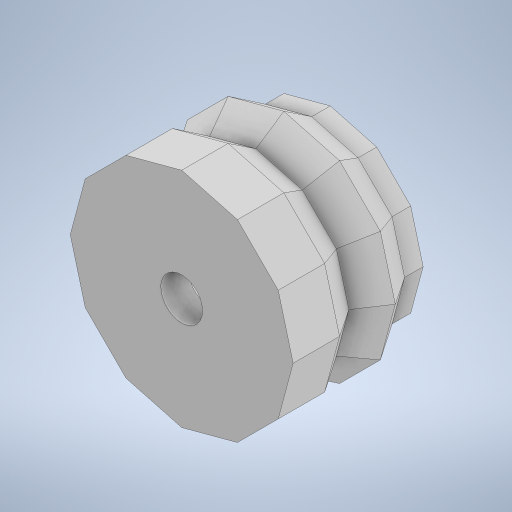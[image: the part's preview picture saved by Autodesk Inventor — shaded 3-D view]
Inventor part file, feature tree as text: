
AUTODESK INVENTOR PART (.ipt)
format: ipt  version: 2023 (Build 270158000, 158)  size: 361,984 bytes
history: native  units: in
note: dims shown in document units (in); Inventor stores cm internally (conversion verified against a paired STEP export)
features: sketch x6, extrude x4, projected_geometry x3, other x2, mirror x2, loft x1, shell x1
ambient origin geometry x8: Origin, YZ Plane, XZ Plane, XY Plane, X Axis, Y Axis, Z Axis, Center Point
bodies: Body1 (feature_tree)
feature tree (19):
  other  "솔리드1"
  sketch  "스케치1"
  other  "작업 평면1"
  loft  "로프트1"
  mirror  "미러1"
  mirror  "미러2"
  extrude  "돌출1"  Depth=0.1181in
  shell  "쉘1"  Thickness=0.7874in
  extrude  "돌출2"  TaperAngle=0.0deg  [1 undecoded]
  extrude  "돌출3"  TaperAngle=0.0deg  [1 undecoded]
  extrude  "돌출4"  Depth=0.0984in TaperAngle=0.0deg
  sketch  "스케치2"
  sketch  "스케치3"
  projected_geometry  "투영된 루프1"
  sketch  "스케치4"
  projected_geometry  "투영된 루프2"
  sketch  "스케치5"
  sketch  "스케치6"
  projected_geometry  "투영된 루프3"
note: 2 required parameter values undecoded (feature->parameter linkage not recoverable at this tier; creation-order binding heuristic only, values carry confidence <= 0.55)
